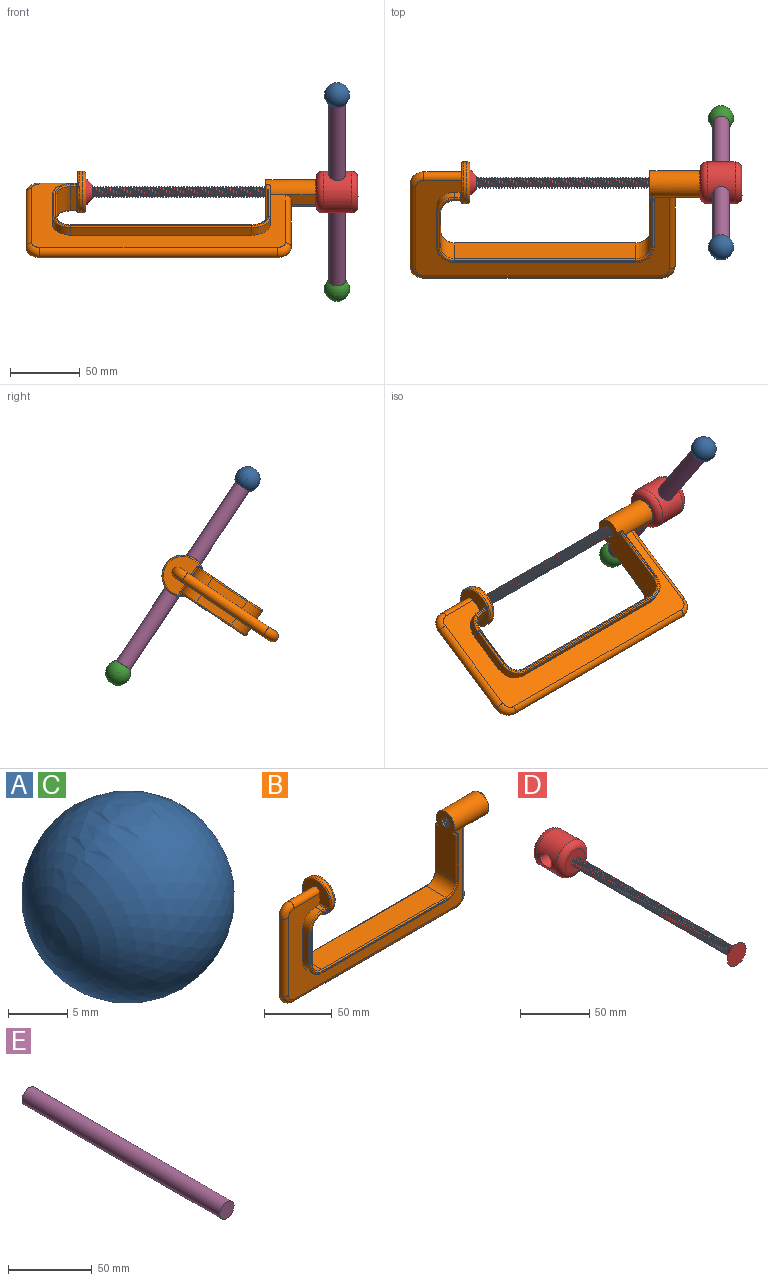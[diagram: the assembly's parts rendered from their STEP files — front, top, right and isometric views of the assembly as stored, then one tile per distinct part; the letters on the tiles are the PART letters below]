
ASSEMBLY  parts=5 mates=4
PART A: 3 faces, bbox 18x18x18 mm
  f0: sphere r=9mm, area 888.3mm2, adj f1
  f1: cylinder r=6mm len=12mm, axis (0,-1,0), area 252.9mm2, adj f0,f2
  f2: plane 12x12mm, normal (0,1,0), area 113.1mm2, adj f1
PART B: 126 faces, bbox 209.8x32.5x98.6 mm
  f0: plane 20.57x4.51mm, normal (-1,0,0), area 64mm2, adj f94,f96,f105
  f1: cylinder r=15mm len=30mm, axis (-1,0,0), area 266.9mm2, adj f101,f102,f103,f104,f105,f106,f107,f118
  f2: plane 18.02x17.13mm, normal (1,0,0), area 191.5mm2, adj f4,f54,f55,f56,f57,f108,f109
  f3: cylinder r=4.19mm len=8.38mm, axis (1,0,0), area 42.6mm2, adj f22,f25,f53,f54,f55
  f4: cylinder r=4.19mm len=8.38mm, axis (1,0,0), area 20.3mm2, adj f2,f5,f54,f55
  f5: cylinder r=4.19mm len=8.38mm, axis (1,0,0), area 29.5mm2, adj f4,f6,f54,f55
  f6: cylinder r=4.19mm len=8.38mm, axis (1,0,0), area 29.5mm2, adj f5,f7,f54,f55
  f7: cylinder r=4.19mm len=8.38mm, axis (1,0,0), area 29.5mm2, adj f6,f8,f54,f55
  f8: cylinder r=4.19mm len=8.38mm, axis (1,0,0), area 29.5mm2, adj f7,f9,f54,f55
  f9: cylinder r=4.19mm len=8.38mm, axis (1,0,0), area 29.5mm2, adj f8,f10,f54,f55
  f10: cylinder r=4.19mm len=8.38mm, axis (1,0,0), area 29.5mm2, adj f9,f11,f54,f55
  f11: cylinder r=4.19mm len=8.38mm, axis (1,0,0), area 29.5mm2, adj f10,f12,f54,f55
  f12: cylinder r=4.19mm len=8.38mm, axis (1,0,0), area 29.5mm2, adj f11,f13,f54,f55
  f13: cylinder r=4.19mm len=8.38mm, axis (1,0,0), area 29.5mm2, adj f12,f14,f54,f55
  f14: cylinder r=4.19mm len=8.38mm, axis (1,0,0), area 29.5mm2, adj f13,f15,f54,f55
  f15: cylinder r=4.19mm len=8.38mm, axis (1,0,0), area 29.5mm2, adj f14,f16,f54,f55
  f16: cylinder r=4.19mm len=8.38mm, axis (1,0,0), area 29.5mm2, adj f15,f17,f54,f55
  f17: cylinder r=4.19mm len=8.38mm, axis (1,0,0), area 29.5mm2, adj f16,f18,f54,f55
  f18: cylinder r=4.19mm len=8.38mm, axis (1,0,0), area 29.5mm2, adj f17,f19,f54,f55
  f19: cylinder r=4.19mm len=8.38mm, axis (1,0,0), area 29.5mm2, adj f18,f20,f54,f55
  f20: cylinder r=4.19mm len=8.38mm, axis (1,0,0), area 29.5mm2, adj f19,f21,f54,f55
  f21: cylinder r=4.19mm len=8.38mm, axis (1,0,0), area 29.5mm2, adj f20,f22,f54,f55
  f22: cylinder r=4.19mm len=8.38mm, axis (1,0,0), area 29.5mm2, adj f3,f21,f54,f55
  f23: plane 2.63x1mm, normal (0,0,1), area 2.6mm2, adj f51,f72,f114,f116
  f24: plane 3.13x1mm, normal (0,0,1), area 3.1mm2, adj f51,f63,f110,f112
  f25: plane 57.04x20.54mm, normal (-1,0,0), area 1036.4mm2, adj f3,f31,f51,f58,f59,f60,f65,f69
  f26: plane 130x20.5mm, normal (0,0,1), area 2665mm2, adj f31,f32,f70,f77
  f27: plane 30x20.5mm, normal (1,0,0), area 615mm2, adj f32,f33,f78,f86
  f28: plane 20.5x4mm, normal (0,0,-1), area 82mm2, adj f33,f87,f93,f94
  f29: plane 182x82mm, normal (0,-1,0), area 4738.1mm2, adj f34,f35,f36,f37,f38,f39,f40,f50
  f30: plane 182x82mm, normal (0,1,0), area 4738.1mm2, adj f42,f43,f44,f45,f46,f47,f48,f50
  f31: cylinder r=10mm len=20.5mm, axis (0,-1,0), area 322mm2, adj f25,f26,f67,f73
  f32: cylinder r=10mm len=20.5mm, axis (0,-1,0), area 322mm2, adj f26,f27,f74,f82
  f33: cylinder r=10mm len=20.5mm, axis (0,-1,0), area 322mm2, adj f27,f28,f83,f90
  f34: cylinder r=13mm len=13mm, axis (0,1,0), area 132.7mm2, adj f29,f35,f40,f64
  f35: plane 40.5x6.5mm, normal (1,0,0), area 261.1mm2, adj f29,f34,f51,f62,f110
  f36: plane 6.5x4mm, normal (0,0,1), area 26mm2, adj f29,f37,f79,f80
  f37: cylinder r=13mm len=13mm, axis (0,1,0), area 132.7mm2, adj f29,f36,f38,f75
  f38: plane 30x6.5mm, normal (-1,0,0), area 195mm2, adj f29,f37,f39,f71
  f39: cylinder r=13mm len=13mm, axis (0,1,0), area 132.7mm2, adj f29,f38,f40,f68
  f40: plane 130x6.5mm, normal (0,0,-1), area 845mm2, adj f29,f34,f39,f66
  f41: plane 154x54mm, normal (0,-1,0), area 258.7mm2, adj f62,f63,f64,f65,f66,f67,f68,f70
  f42: plane 6x4mm, normal (0,0,1), area 24mm2, adj f30,f48,f97,f100
  f43: plane 40.5x6mm, normal (1,0,0), area 240.8mm2, adj f30,f44,f51,f76,f114
  f44: cylinder r=13mm len=13mm, axis (0,-1,0), area 122.5mm2, adj f30,f43,f45,f81
  f45: plane 130x6mm, normal (0,0,-1), area 780mm2, adj f30,f44,f46,f85
  f46: cylinder r=13mm len=13mm, axis (0,-1,0), area 122.5mm2, adj f30,f45,f47,f89
  f47: plane 30x6mm, normal (-1,0,0), area 180mm2, adj f30,f46,f48,f92
  f48: cylinder r=13mm len=13mm, axis (0,-1,0), area 122.5mm2, adj f30,f42,f47,f95
  f49: plane 154x54mm, normal (0,1,0), area 258.7mm2, adj f69,f72,f73,f76,f77,f81,f82,f85
  f50: plane 28x21mm, normal (-1,0,0), area 338.8mm2, adj f29,f30,f80,f84,f88,f98,f99,f100
  f51: cylinder r=9.5mm len=35.5mm, axis (1,0,0), area 1802.8mm2, adj f23,f24,f25,f29,f30,f35,f43,f52
  f52: plane 21.5x8mm, normal (0,0,-1), area 146.9mm2, adj f51,f109,f125
  f53: plane 0.68x0.55mm, normal (0,-0.36,-0.93), area 0.2mm2, adj f3,f54,f55
  f54: bspline ~36.5x10.28mm, area 309.7mm2, adj f2,f3,f4,f5,f6,f7,f8,f9
  f55: bspline ~36.5x10.28mm, area 324.2mm2, adj f2,f3,f4,f5,f6,f7,f8,f9
  f56: cylinder r=4.45mm len=8.9mm, axis (1,0,0), area 6.2mm2, adj f2,f55,f57
  f57: plane 0.9x0.81mm, normal (0,0.36,0.93), area 0.4mm2, adj f2,f54,f55,f56
  f58: bspline ~3.9x2.87mm, area 0.2mm2, adj f25,f59,f60
  f59: cylinder r=4.45mm len=1.63mm, axis (1,0,0), area 0.1mm2, adj f25,f58,f60
  f60: plane 0.17x0.11mm, normal (0,-0.36,-0.93), area 0mm2, adj f25,f58,f59
  f61: plane 25.65x25.65mm, normal (1,0,0), area 516.9mm2, adj f118
  f62: cylinder r=1mm len=40.5mm, axis (0,0,-1), area 63.6mm2, adj f35,f41,f64,f111
  f63: cylinder r=1mm len=1mm, axis (1,0,0), area 1.6mm2, adj f24,f41,f111,f113
  f64: torus R=12mm, axis (0,-1,0), area 31.2mm2, adj f34,f41,f62,f66
  f65: cylinder r=1mm len=40.5mm, axis (0,0,1), area 63.6mm2, adj f25,f41,f67,f113
  f66: cylinder r=1mm len=130mm, axis (-1,0,0), area 204.2mm2, adj f40,f41,f64,f68
  f67: torus R=11mm, axis (0,-1,0), area 25.6mm2, adj f31,f41,f65,f70
  f68: torus R=12mm, axis (0,-1,0), area 31.2mm2, adj f39,f41,f66,f71
  f69: cylinder r=1mm len=40.5mm, axis (0,0,1), area 63.6mm2, adj f25,f49,f73,f117
  f70: cylinder r=1mm len=130mm, axis (1,0,0), area 204.2mm2, adj f26,f41,f67,f74
  f71: cylinder r=1mm len=30mm, axis (0,0,1), area 47.1mm2, adj f38,f41,f68,f75
  f72: cylinder r=1mm len=1mm, axis (1,0,0), area 1.6mm2, adj f23,f49,f115,f117
  f73: torus R=11mm, axis (0,1,0), area 25.6mm2, adj f31,f49,f69,f77
  f74: torus R=11mm, axis (0,-1,0), area 25.6mm2, adj f32,f41,f70,f78
  f75: torus R=12mm, axis (0,-1,0), area 31.2mm2, adj f37,f41,f71,f79
  f76: cylinder r=1mm len=40.5mm, axis (0,0,1), area 63.6mm2, adj f43,f49,f81,f115
  f77: cylinder r=1mm len=130mm, axis (1,0,0), area 204.2mm2, adj f26,f49,f73,f82
  f78: cylinder r=1mm len=30mm, axis (0,0,-1), area 47.1mm2, adj f27,f41,f74,f83
  f79: cylinder r=1mm len=4mm, axis (1,0,0), area 6.3mm2, adj f36,f41,f75,f84
  f80: cylinder r=1mm len=6.5mm, axis (0,-1,0), area 10.2mm2, adj f29,f36,f50,f84
  f81: torus R=12mm, axis (0,1,0), area 31.2mm2, adj f44,f49,f76,f85
  f82: torus R=11mm, axis (0,1,0), area 25.6mm2, adj f32,f49,f77,f86
  f83: torus R=11mm, axis (0,-1,0), area 25.6mm2, adj f33,f41,f78,f87
  f84: torus R=2mm, axis (1,0,0), area 3.4mm2, adj f50,f79,f80,f88
  f85: cylinder r=1mm len=130mm, axis (1,0,0), area 204.2mm2, adj f45,f49,f81,f89
  f86: cylinder r=1mm len=30mm, axis (0,0,-1), area 47.1mm2, adj f27,f49,f82,f90
  f87: cylinder r=1mm len=4mm, axis (-1,0,0), area 6.3mm2, adj f28,f41,f83,f91
  f88: cylinder r=1mm len=1mm, axis (0,0,-1), area 1.4mm2, adj f41,f50,f84,f91,f102
  f89: torus R=12mm, axis (0,1,0), area 31.2mm2, adj f46,f49,f85,f92
  f90: torus R=11mm, axis (0,1,0), area 25.6mm2, adj f33,f49,f86,f93
  f91: torus R=2mm, axis (1,0,0), area 2.4mm2, adj f87,f88,f94,f101
  f92: cylinder r=1mm len=30mm, axis (0,0,-1), area 47.1mm2, adj f47,f49,f89,f95
  f93: cylinder r=1mm len=4mm, axis (-1,0,0), area 6.3mm2, adj f28,f49,f90,f96
  f94: cylinder r=1mm len=20.5mm, axis (0,1,0), area 32.2mm2, adj f0,f28,f91,f96,f103
  f95: torus R=12mm, axis (0,1,0), area 31.2mm2, adj f48,f49,f92,f97
  f96: torus R=2mm, axis (1,0,0), area 2.7mm2, adj f0,f93,f94,f98,f107
  f97: cylinder r=1mm len=4mm, axis (-1,0,0), area 6.3mm2, adj f42,f49,f95,f99
  f98: cylinder r=1mm len=1mm, axis (0,0,-1), area 1.5mm2, adj f49,f50,f96,f99,f106
  f99: torus R=2mm, axis (1,0,0), area 3.4mm2, adj f50,f97,f98,f100
  f100: cylinder r=1mm len=6mm, axis (0,-1,0), area 9.4mm2, adj f30,f42,f50,f99
  f101: bspline ~3.18x2.77mm, area 3.3mm2, adj f1,f91,f102,f103
  f102: bspline ~3.1x1.88mm, area 1.6mm2, adj f1,f88,f101,f104
  f103: bspline ~1.21x1.07mm, area 0.2mm2, adj f1,f94,f101,f105
  f104: torus R=14mm, axis (1,0,0), area 95.5mm2, adj f1,f50,f102,f106
  f105: torus R=14mm, axis (1,0,0), area 37.9mm2, adj f0,f1,f103,f107
  f106: bspline ~2.29x1.67mm, area 0.8mm2, adj f1,f98,f104,f107
  f107: bspline ~3.24x2.8mm, area 3.7mm2, adj f1,f96,f105,f106
  f108: torus R=9mm, axis (1,0,0), area 39.5mm2, adj f2,f51,f109
  f109: cylinder r=0.5mm len=8mm, axis (0,1,0), area 6.2mm2, adj f2,f52,f108
  f110: cylinder r=1mm len=4.08mm, axis (0,1,0), area 5.7mm2, adj f24,f35,f51,f111
  f111: sphere r=1mm, area 1.6mm2, adj f62,f63,f110
  f112: cylinder r=1mm len=4.08mm, axis (0,-1,0), area 5.7mm2, adj f24,f25,f51,f113
  f113: sphere r=1mm, area 1.6mm2, adj f63,f65,f112
  f114: cylinder r=1mm len=3.58mm, axis (0,1,0), area 4.9mm2, adj f23,f43,f51,f115
  f115: sphere r=1mm, area 1mm2, adj f72,f76,f114
  f116: cylinder r=1mm len=3.58mm, axis (0,-1,0), area 4.9mm2, adj f23,f25,f51,f117
  f117: sphere r=1mm, area 2.1mm2, adj f69,f72,f116
  f118: torus R=12.83mm, axis (1,0,0), area 304.7mm2, adj f1,f61
  f119: cylinder r=4mm len=27mm, axis (-1,0,0), area 339.3mm2, adj f29,f30,f50,f120
  f120: torus R=6mm, axis (0,-1,0), area 168.7mm2, adj f29,f30,f119,f121
  f121: cylinder r=4mm len=70mm, axis (0,0,-1), area 879.6mm2, adj f29,f30,f120,f122
  f122: torus R=6mm, axis (0,-1,0), area 168.7mm2, adj f29,f30,f121,f123
  f123: cylinder r=4mm len=170mm, axis (1,0,0), area 2136.3mm2, adj f29,f30,f122,f124
  f124: torus R=6mm, axis (0,-1,0), area 168.7mm2, adj f29,f30,f123,f125
  f125: cylinder r=4mm len=61.88mm, axis (0,0,1), area 777.6mm2, adj f29,f30,f52,f124
PART C: same geometry as A
PART D: 13 faces, bbox 32.5x195x32.5 mm
  f0: bspline ~160.5x8.93mm, area 1729.7mm2, adj f1,f3,f4,f10
  f1: bspline ~160.17x8.93mm, area 1724.5mm2, adj f0,f3,f4,f10
  f2: cylinder r=15mm len=30mm, axis (0,-1,0), area 1654mm2, adj f7,f8,f9
  f3: cylinder r=3mm len=160mm, axis (0,1,0), area 2093.7mm2, adj f0,f1,f4,f5,f10
  f4: plane 1x0.87mm, normal (0,0,1), area 0.4mm2, adj f0,f1,f3
  f5: plane 20x20mm, normal (0,-1,0), area 285.9mm2, adj f3,f8
  f6: plane 20x20mm, normal (0,1,0), area 314.2mm2, adj f9
  f7: cylinder r=6mm len=30mm, axis (-1,0,0), area 1084.3mm2, adj f2
  f8: torus R=10mm, axis (0,1,0), area 650.6mm2, adj f2,f5
  f9: torus R=10mm, axis (0,1,0), area 650.6mm2, adj f2,f6
  f10: plane 9x9mm, normal (0,1,0), area 30.9mm2, adj f0,f1,f3,f12
  f11: plane 19x19mm, normal (0,-1,0), area 283.5mm2, adj f12
  f12: cone r=14.5mm half-angle=45deg, axis (0,-1,0), area 311mm2, adj f10,f11
PART E: 3 faces, bbox 12x167x12 mm
  f0: cylinder r=6mm len=167mm, axis (0,1,0), area 6295.8mm2, adj f1,f2
  f1: plane 12x12mm, normal (0,-1,0), area 113.1mm2, adj f0
  f2: plane 12x12mm, normal (0,1,0), area 113.1mm2, adj f0
PLACE A rot(axis=(0,0.88,-0.47),180deg) t=(-67.85,-95.39,138.64)mm
PLACE B rot(axis=(-1,0,0),56.3deg) t=(-253.85,-41.91,73.79)mm
PLACE C rot(axis=(1,0,0),123.7deg) t=(-67.85,-2.71,-0.28)mm
PLACE D rot(axis=(0.66,0.66,-0.35),141deg) t=(-82.85,-49.05,69.18)mm
PLACE E rot(axis=(1,0,0),123.7deg) t=(-67.85,-95.39,138.64)mm
MATE cylindrical D.f12 <-> B.f1  axis (-1,0,0) through (-247.85,-49.05,69.18)mm
MATE fastened C.f1 <-> E.f0  axis (0,-0.56,0.83) through (-67.85,-2.71,-0.28)mm
MATE fastened A.f1 <-> E.f0  axis (0,0.56,-0.83) through (-67.85,-95.39,138.64)mm
MATE revolute E.f0 <-> D.f7  axis (0,-0.56,0.83) through (-67.85,-49.05,69.18)mm
